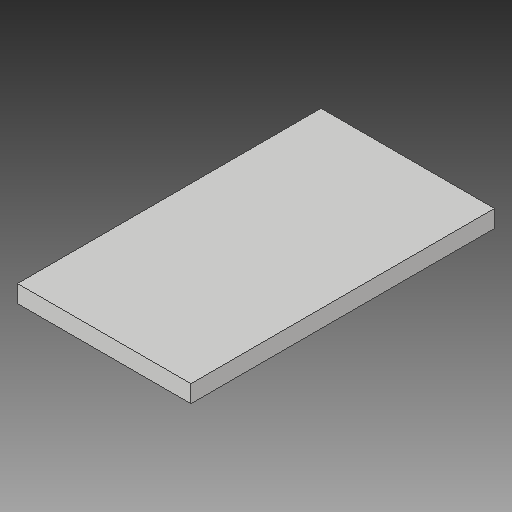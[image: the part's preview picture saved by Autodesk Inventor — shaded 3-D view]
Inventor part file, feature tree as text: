
AUTODESK INVENTOR PART (.ipt)
format: ipt  version: 2019 (Build 230136000, 136)  size: 87,040 bytes
history: native  units: in
note: dims shown in document units (in); Inventor stores cm internally (conversion verified against a paired STEP export)
features: other x3, sketch x2
ambient origin geometry x8: Origin, YZ Plane, XZ Plane, XY Plane, X Axis, Y Axis, Z Axis, Center Point
bodies: Solid1 (feature_tree)
feature tree (5):
  other  "Cap1.ipt"
  other  "Solid1::Cap1.ipt"
  other  "TaggingFeature1"
  sketch  "Sketch1"  dims[d0=0.3937in]
  sketch  "Sketch2"
